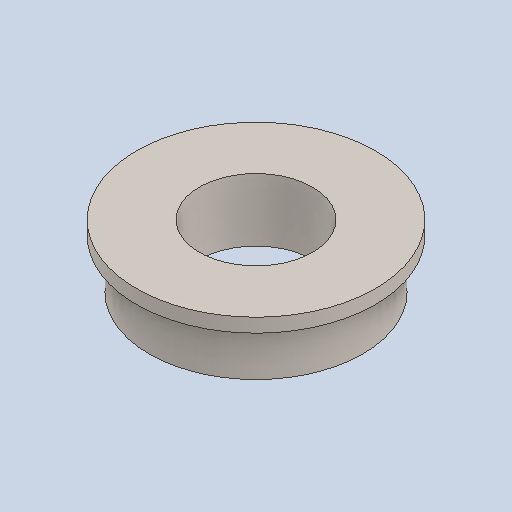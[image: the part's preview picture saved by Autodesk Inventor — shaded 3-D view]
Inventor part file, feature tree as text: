
AUTODESK INVENTOR PART (.ipt)
format: ipt  version: 2023.2 (Build 272271000, 271)  size: 105,472 bytes
history: native  units: in
note: dims shown in document units (in); Inventor stores cm internally (conversion verified against a paired STEP export)
features: revolve x1
ambient origin geometry x8: Origin, YZ Plane, XZ Plane, XY Plane, X Axis, Y Axis, Z Axis, Center Point
bodies: Solid1 (feature_tree)
feature tree (1):
  revolve  "Revolve1"  [1 undecoded]
note: 1 required parameter value undecoded (feature->parameter linkage not recoverable at this tier; creation-order binding heuristic only, values carry confidence <= 0.55)
